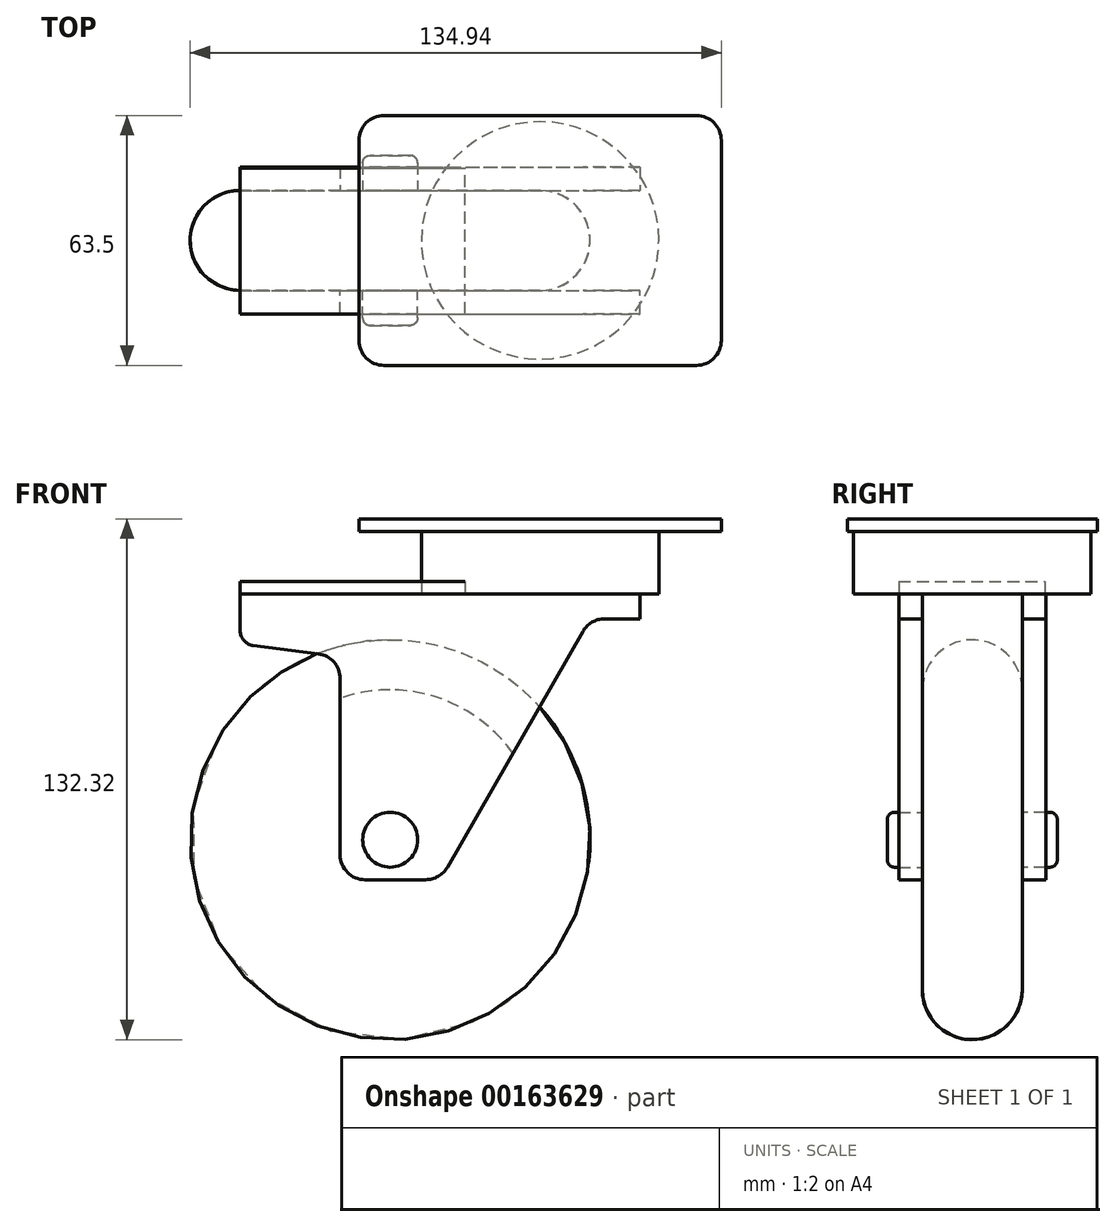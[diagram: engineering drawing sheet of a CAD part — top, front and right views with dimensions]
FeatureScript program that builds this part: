
annotation { "Feature Type Name" : "Feature", "Feature Type Description" : "" }
export const myFeature = defineFeature(function(context is Context, id is Id, definition is map)
    precondition{}
    {
        {
            var Q0;
            Q0=qCreatedBy(makeId("Right.planeOp"),FACE);
            var sketch = newSketch(context, id + "F0", { "sketchPlane" : qUnion([Q0])});
            skLineSegment(sketch, "E0.bottom", {"start": v(0, 0) * mm, "end": v(12.7, 0) * mm});
            skLineSegment(sketch, "E0.top", {"start": v(0, 50.8) * mm, "end": v(0, 50.8) * mm});
            skLineSegment(sketch, "E0.left", {"start": v(0, 0) * mm, "end": v(0, 50.8) * mm});
            skLineSegment(sketch, "E0.right", {"start": v(12.7, 0) * mm, "end": v(12.7, 38.1) * mm});
            skPoint(sketch, "E1.visualSharp", {"position": v(12.7, 50.8) * mm});
            skArc(sketch, "E1.filletArc", {"start": v(12.7, 38.1) * mm, "mid": v(8.98, 47.08) * mm, "end": v(0, 50.8) * mm});
            skLineSegment(sketch, "E2", {"start": v(0, 0) * mm, "end": v(29.52, 0) * mm, "construction": true});
            skPoint(sketch, "E2.endSnap0", {"position": v(6.35, 0) * mm});
            skLineSegment(sketch, "E3.MirrorCS", {"start": v(0, 0) * mm, "end": v(-12.7, 0) * mm});
            skLineSegment(sketch, "E4.MirrorCS", {"start": v(-12.7, 0) * mm, "end": v(-12.7, 38.1) * mm});
            skArc(sketch, "E5.MirrorCS", {"start": v(-12.7, 38.1) * mm, "mid": v(-8.98, 47.08) * mm, "end": v(0, 50.8) * mm});
            skLineSegment(sketch, "E6.MirrorCS", {"start": v(0, 0) * mm, "end": v(-29.52, 0) * mm, "construction": true});
            skSolve(sketch);
        }
        {
            var Q0;
            Q0=makeQuery(id+"F0.imprint","IMPRINT",FACE,{"disambiguationData":[TD([[makeQuery(id+"F0.imprint","IMPRINT",EDGE,{"derivedFrom":sQuery(id+"F0.wireOp",EDGE,"E0.left")}),1.0]])]});
            var Q1;
            Q1=makeQuery(id+"F0.imprint","IMPRINT",FACE,{"disambiguationData":[TD([[makeQuery(id+"F0.imprint","IMPRINT",EDGE,{"derivedFrom":sQuery(id+"F0.wireOp",EDGE,"E0.bottom")}),1.0]])]});
            var Q2;
            Q2=sQuery(id+"F0.wireOp",EDGE,"E6.MirrorCS");
            revolve(context, id + "F1", {"entities" : qUnion([Q0, Q1]), "axis" : qUnion([Q2]), "revolveType" : RevolveType.FULL});
        }
        {
            var Q0;
            Q0=makeQuery(id+"F1.opRevolve","SWEPT_FACE",FACE,{"disambiguationData":[OSD([sQuery(id+"F0.wireOp",EDGE,"E4.MirrorCS")])]});
            var sketch = newSketch(context, id + "F2", { "sketchPlane" : qUnion([Q0])});
            skCircle(sketch, "E7", {"center": v(0, 0) * mm, "radius": 6.99 * mm});
            skSolve(sketch);
        }
        {
            var Q0;
            Q0 = qSketchRegion(id + "F2", true);
            extrude(context, id + "F3", {"entities" : qUnion([Q0]), "operationType" : NewBodyOperationType.ADD, "depth" : 8.9 * mm});
        }
        {
            var Q0;
            Q0=makeQuery(id+"F3.opExtrude","CAP_EDGE",EDGE,{"disambiguationData":[OSD([sQuery(id+"F2.wireOp",EDGE,"E7")])],"isStart":false});
            fillet(context, id + "F4", {"entities" : qUnion([Q0]), "radius" : 1.96 * mm, "tangentPropagation" : true, "allowEdgeOverflow" : false});
        }
        {
            var Q0;
            Q0=makeQuery(id+"F1.opRevolve","SWEPT_FACE",FACE,{"disambiguationData":[OSD([sQuery(id+"F0.wireOp",EDGE,"E0.right")])]});
            var sketch = newSketch(context, id + "F5", { "sketchPlane" : qUnion([Q0])});
            skCircle(sketch, "E8", {"center": v(0, 0) * mm, "radius": 6.99 * mm});
            skSolve(sketch);
        }
        {
            var Q0;
            Q0 = qSketchRegion(id + "F5", true);
            extrude(context, id + "F6", {"entities" : qUnion([Q0]), "operationType" : NewBodyOperationType.ADD, "depth" : 8.9 * mm});
        }
        {
            var Q0;
            Q0=makeQuery(id+"F6.opExtrude","CAP_FACE",FACE,{"disambiguationData":[OSD([sQuery(id+"F5.wireOp",EDGE,"E8")])],"isStart":false});
            fillet(context, id + "F7", {"entities" : qUnion([Q0]), "radius" : 1.84 * mm, "tangentPropagation" : true, "allowEdgeOverflow" : false});
        }
        {
            var Q0;
            Q0=makeQuery(id+"F1.opRevolve","SWEPT_FACE",FACE,{"disambiguationData":[OSD([sQuery(id+"F0.wireOp",EDGE,"E4.MirrorCS")])]});
            var sketch = newSketch(context, id + "F8", { "sketchPlane" : qUnion([Q0])});
            skLineSegment(sketch, "E9.top", {"start": v(0, 62.47) * mm, "end": v(12.7, 62.47) * mm});
            skLineSegment(sketch, "E9.left", {"start": v(0, 0) * mm, "end": v(0, 62.47) * mm, "construction": true});
            skLineSegment(sketch, "E9.right", {"start": v(12.7, 0) * mm, "end": v(12.7, 62.47) * mm});
            skLineSegment(sketch, "E10.top", {"start": v(1.75, 62.47) * mm, "end": v(-12.7, 62.47) * mm});
            skLineSegment(sketch, "E10.right", {"start": v(-12.7, 0) * mm, "end": v(-12.7, 40.93) * mm});
            skLineSegment(sketch, "E11.top", {"start": v(-6.35, -10.16) * mm, "end": v(9.03, -10.16) * mm});
            skLineSegment(sketch, "E11.left", {"start": v(-12.7, 0) * mm, "end": v(-12.7, -3.81) * mm});
            skLineSegment(sketch, "E11.right", {"start": v(12.7, 0) * mm, "end": v(12.7, -10.16) * mm});
            skPoint(sketch, "E12.visualSharp", {"position": v(-12.7, -10.16) * mm});
            skArc(sketch, "E12.filletArc", {"start": v(-12.7, -3.81) * mm, "mid": v(-10.84, -8.3) * mm, "end": v(-6.35, -10.16) * mm});
            skLineSegment(sketch, "E13", {"start": v(0, 62.47) * mm, "end": v(-38.1, 62.47) * mm});
            skLineSegment(sketch, "E14", {"start": v(-38.1, 62.47) * mm, "end": v(-38.1, 53.12) * mm});
            skLineSegment(sketch, "E15", {"start": v(-34.77, 49.34) * mm, "end": v(-18.24, 47.23) * mm});
            skLineSegment(sketch, "E16", {"start": v(12.7, 62.47) * mm, "end": v(63.5, 62.47) * mm});
            skLineSegment(sketch, "E17", {"start": v(63.5, 62.47) * mm, "end": v(63.5, 56.12) * mm});
            skLineSegment(sketch, "E18", {"start": v(63.5, 56.12) * mm, "end": v(54.47, 56.12) * mm});
            skLineSegment(sketch, "E19", {"start": v(14.53, -6.97) * mm, "end": v(48.97, 52.94) * mm});
            skPoint(sketch, "E20.visualSharp", {"position": v(12.7, -10.16) * mm});
            skArc(sketch, "E20.filletArc", {"start": v(9.03, -10.16) * mm, "mid": v(12.2, -9.3) * mm, "end": v(14.53, -6.97) * mm});
            skArc(sketch, "E21.filletArc", {"start": v(-12.7, 40.93) * mm, "mid": v(-14.28, 45.13) * mm, "end": v(-18.24, 47.23) * mm});
            skPoint(sketch, "E22.visualSharp", {"position": v(-38.1, 49.77) * mm});
            skArc(sketch, "E22.filletArc", {"start": v(-38.1, 53.12) * mm, "mid": v(-37.15, 50.6) * mm, "end": v(-34.77, 49.34) * mm});
            skPoint(sketch, "E23.visualSharp", {"position": v(50.8, 56.12) * mm});
            skArc(sketch, "E23.filletArc", {"start": v(54.47, 56.12) * mm, "mid": v(51.3, 55.27) * mm, "end": v(48.97, 52.94) * mm});
            skSolve(sketch);
        }
        {
            var Q0;
            Q0 = qSketchRegion(id + "F8", true);
            extrude(context, id + "F9", {"entities" : qUnion([Q0]), "operationType" : NewBodyOperationType.ADD, "depth" : 5.97 * mm});
        }
        {
            var Q0;
            Q0=makeQuery(id+"F1.opRevolve","SWEPT_BODY",BODY,{"disambiguationData":[OSD([sQuery(id+"F0.wireOp",EDGE,"E0.bottom"),sQuery(id+"F0.wireOp",EDGE,"E0.right"),sQuery(id+"F0.wireOp",EDGE,"E1.filletArc"),sQuery(id+"F0.wireOp",EDGE,"E3.MirrorCS"),sQuery(id+"F0.wireOp",EDGE,"E4.MirrorCS"),sQuery(id+"F0.wireOp",EDGE,"E5.MirrorCS")])]});
            var Q1;
            Q1=qCreatedBy(makeId("Front.planeOp"),FACE);
            mirror(context, id + "F10", {"entities" : qUnion([Q0]), "mirrorPlane" : qUnion([Q1])});
        }
        {
            var Q0;
            Q0=makeQuery(id+"F9.opExtrude","SWEPT_FACE",FACE,{"disambiguationData":[OSD([sQuery(id+"F8.wireOp",EDGE,"E9.top"),sQuery(id+"F8.wireOp",EDGE,"E10.top"),sQuery(id+"F8.wireOp",EDGE,"E13"),sQuery(id+"F8.wireOp",EDGE,"E16")])]});
            var sketch = newSketch(context, id + "F11", { "sketchPlane" : qUnion([Q0])});
            skLineSegment(sketch, "E24", {"start": v(0, 0) * mm, "end": v(38.1, 0) * mm, "construction": true});
            skCircle(sketch, "E25", {"center": v(38.1, 0) * mm, "radius": 30.16 * mm});
            skSolve(sketch);
        }
        {
            var Q0;
            {var subQ0=sQuery(id+"F11.wireOp",EDGE,"E25");var subQ1=sQuery(id+"F8.wireOp",EDGE,"E16");var subQ4=makeQuery(id+"F9.opExtrude","SWEPT_EDGE",EDGE,{"disambiguationData":[OSD([subQ1,sQuery(id+"F8.wireOp",EDGE,"E17")])]});var subQ5=makeQuery(id+"F11.imprint","INTERSECT",VERTEX,{"derivedFrom":[subQ4,subQ0]});Q0=makeQuery(id+"F11.imprint","IMPRINT",FACE,{"disambiguationData":[TD([[makeQuery(id+"F11.imprint","IMPRINT",EDGE,{"disambiguationData":[TD([[subQ5,-1.0]])],"derivedFrom":subQ0}),1.0]])]});}
            var Q1;
            {var subQ0=sQuery(id+"F8.wireOp",EDGE,"E16");var subQ5=makeQuery(id+"F9.opExtrude","SWEPT_EDGE",EDGE,{"disambiguationData":[OSD([subQ0,sQuery(id+"F8.wireOp",EDGE,"E17")])]});var subQ7=sQuery(id+"F11.wireOp",EDGE,"E25");var subQ9=makeQuery(id+"F11.imprint","INTERSECT",VERTEX,{"derivedFrom":[subQ5,subQ7]});Q1=makeQuery(id+"F11.imprint","IMPRINT",FACE,{"disambiguationData":[TD([[makeQuery(id+"F11.imprint","IMPRINT",EDGE,{"disambiguationData":[TD([[subQ9,1.0]])],"derivedFrom":subQ7}),1.0]])]});}
            var Q2;
            {var subQ0=sQuery(id+"F11.wireOp",EDGE,"E25");var subQ1=makeQuery(id+"F9.opExtrude","CAP_EDGE",EDGE,{"disambiguationData":[OSD([sQuery(id+"F8.wireOp",EDGE,"E9.top"),sQuery(id+"F8.wireOp",EDGE,"E10.top"),sQuery(id+"F8.wireOp",EDGE,"E13"),sQuery(id+"F8.wireOp",EDGE,"E16")])],"isStart":false});var subQ2=makeQuery(id+"F11.imprint","INTERSECT",VERTEX,{"disambiguationData":[OD(0.0)],"derivedFrom":[subQ1,subQ0]});Q2=makeQuery(id+"F11.imprint","IMPRINT",FACE,{"disambiguationData":[TD([[makeQuery(id+"F11.imprint","IMPRINT",EDGE,{"disambiguationData":[TD([[subQ2,-1.0]])],"derivedFrom":subQ0}),1.0]])]});}
            var Q3;
            Q3=sQuery(id+"F11.wireOp",EDGE,"E25");
            extrude(context, id + "F12", {"entities" : qUnion([Q0, Q1, Q2]), "surfaceEntities" : qUnion([Q3]), "depth" : 19.05 * mm});
        }
        {
            var Q0;
            Q0=makeQuery(id+"F12.opExtrude","CAP_FACE",FACE,{"disambiguationData":[OSD([sQuery(id+"F11.wireOp",EDGE,"E25")])],"isStart":false});
            var sketch = newSketch(context, id + "F13", { "sketchPlane" : qUnion([Q0])});
            skLineSegment(sketch, "E26.bottom", {"start": v(77.79, -31.75) * mm, "end": v(-1.59, -31.75) * mm});
            skLineSegment(sketch, "E26.top", {"start": v(77.79, 31.75) * mm, "end": v(-1.59, 31.75) * mm});
            skLineSegment(sketch, "E26.left", {"start": v(84.14, -25.4) * mm, "end": v(84.14, 25.4) * mm});
            skLineSegment(sketch, "E26.right", {"start": v(-7.94, -25.4) * mm, "end": v(-7.94, 25.4) * mm});
            skPoint(sketch, "E26.middle", {"position": v(38.1, 0) * mm});
            skPoint(sketch, "E27.visualSharp", {"position": v(84.14, 31.75) * mm});
            skArc(sketch, "E27.filletArc", {"start": v(84.14, 25.4) * mm, "mid": v(82.28, 29.9) * mm, "end": v(77.79, 31.75) * mm});
            skPoint(sketch, "E28.visualSharp", {"position": v(84.14, -31.75) * mm});
            skArc(sketch, "E28.filletArc", {"start": v(77.79, -31.75) * mm, "mid": v(82.28, -29.9) * mm, "end": v(84.14, -25.4) * mm});
            skPoint(sketch, "E29.visualSharp", {"position": v(-7.94, -31.75) * mm});
            skArc(sketch, "E29.filletArc", {"start": v(-7.94, -25.4) * mm, "mid": v(-6.08, -29.9) * mm, "end": v(-1.59, -31.75) * mm});
            skPoint(sketch, "E30.visualSharp", {"position": v(-7.94, 31.75) * mm});
            skArc(sketch, "E30.filletArc", {"start": v(-1.59, 31.75) * mm, "mid": v(-6.08, 29.9) * mm, "end": v(-7.94, 25.4) * mm});
            skSolve(sketch);
        }
        {
            var Q0;
            Q0 = qSketchRegion(id + "F13", true);
            extrude(context, id + "F14", {"entities" : qUnion([Q0]), "operationType" : NewBodyOperationType.ADD, "oppositeDirection" : true, "depth" : 3.17 * mm});
        }
        {
            var Q0;
            Q0=makeQuery(id+"F9.opExtrude","SWEPT_FACE",FACE,{"disambiguationData":[OSD([sQuery(id+"F8.wireOp",EDGE,"E9.top"),sQuery(id+"F8.wireOp",EDGE,"E10.top"),sQuery(id+"F8.wireOp",EDGE,"E13"),sQuery(id+"F8.wireOp",EDGE,"E16")])]});
            var sketch = newSketch(context, id + "F15", { "sketchPlane" : qUnion([Q0])});
            skLineSegment(sketch, "E31.bottom", {"start": v(-38.1, -18.67) * mm, "end": v(19.05, -18.67) * mm});
            skLineSegment(sketch, "E31.top", {"start": v(-38.1, 18.42) * mm, "end": v(19.05, 18.42) * mm});
            skLineSegment(sketch, "E31.left", {"start": v(-38.1, -18.67) * mm, "end": v(-38.1, 18.42) * mm});
            skLineSegment(sketch, "E31.right", {"start": v(19.05, -18.67) * mm, "end": v(19.05, 18.42) * mm});
            skSolve(sketch);
        }
        {
            var Q0;
            Q0 = qSketchRegion(id + "F15", true);
            extrude(context, id + "F16", {"entities" : qUnion([Q0]), "depth" : 3.17 * mm});
        }
    });
